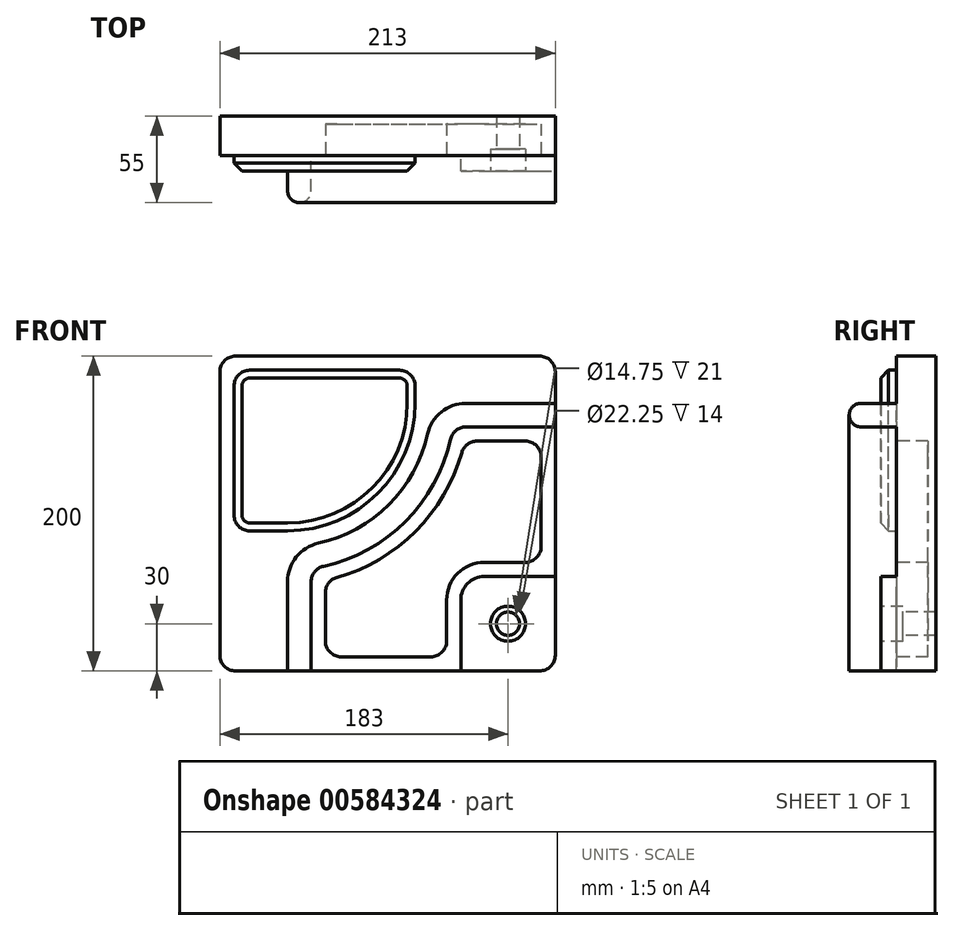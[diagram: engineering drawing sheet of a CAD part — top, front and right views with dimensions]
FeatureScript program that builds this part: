
annotation { "Feature Type Name" : "Feature", "Feature Type Description" : "" }
export const myFeature = defineFeature(function(context is Context, id is Id, definition is map)
    precondition{}
    {
        {
            var Q0;
            Q0=qCreatedBy(makeId("Front.planeOp"),FACE);
            var sketch = newSketch(context, id + "F0", { "sketchPlane" : qUnion([Q0])});
            skLineSegment(sketch, "E0.bottom", {"start": v(-96.5, 100) * mm, "end": v(96.5, 100) * mm});
            skLineSegment(sketch, "E0.top", {"start": v(-96.5, -100) * mm, "end": v(96.5, -100) * mm});
            skLineSegment(sketch, "E0.left", {"start": v(-106.5, 90) * mm, "end": v(-106.5, -90) * mm});
            skLineSegment(sketch, "E0.right", {"start": v(106.5, 90) * mm, "end": v(106.5, -90) * mm});
            skPoint(sketch, "E1.visualSharp", {"position": v(-106.5, -100) * mm});
            skArc(sketch, "E1.filletArc", {"start": v(-106.5, -90) * mm, "mid": v(-103.57, -97.07) * mm, "end": v(-96.5, -100) * mm});
            skPoint(sketch, "E2.visualSharp", {"position": v(106.5, 100) * mm});
            skArc(sketch, "E2.filletArc", {"start": v(106.5, 90) * mm, "mid": v(103.57, 97.07) * mm, "end": v(96.5, 100) * mm});
            skPoint(sketch, "E3.visualSharp", {"position": v(-106.5, 100) * mm});
            skArc(sketch, "E3.filletArc", {"start": v(-96.5, 100) * mm, "mid": v(-103.57, 97.07) * mm, "end": v(-106.5, 90) * mm});
            skPoint(sketch, "E4.visualSharp", {"position": v(106.5, -100) * mm});
            skArc(sketch, "E4.filletArc", {"start": v(96.5, -100) * mm, "mid": v(103.57, -97.07) * mm, "end": v(106.5, -90) * mm});
            skLineSegment(sketch, "E5", {"start": v(106.5, -90) * mm, "end": v(106.5, -91) * mm});
            skLineSegment(sketch, "E6", {"start": v(-106.5, -90) * mm, "end": v(-106.5, -100) * mm});
            skLineSegment(sketch, "E7", {"start": v(-96.5, -100) * mm, "end": v(-106.5, -100) * mm});
            skLineSegment(sketch, "E8", {"start": v(106.5, 90) * mm, "end": v(106.5, -91) * mm});
            skLineSegment(sketch, "E9", {"start": v(-96.5, -100) * mm, "end": v(97.5, -100) * mm});
            skLineSegment(sketch, "E10.bottom", {"start": v(61.5, -40) * mm, "end": v(106.5, -40) * mm});
            skLineSegment(sketch, "E10.top", {"start": v(46.5, -100) * mm, "end": v(97.5, -100) * mm});
            skLineSegment(sketch, "E10.left", {"start": v(46.5, -55) * mm, "end": v(46.5, -100) * mm});
            skLineSegment(sketch, "E10.right", {"start": v(106.5, -40) * mm, "end": v(106.5, -91) * mm});
            skPoint(sketch, "E11.visualSharp", {"position": v(46.5, -40) * mm});
            skArc(sketch, "E11.filletArc", {"start": v(61.5, -40) * mm, "mid": v(50.9, -44.4) * mm, "end": v(46.5, -55) * mm});
            skLineSegment(sketch, "E12", {"start": v(106.5, 70) * mm, "end": v(49.77, 70) * mm});
            skLineSegment(sketch, "E13", {"start": v(-63.5, -100) * mm, "end": v(-63.5, -43.27) * mm});
            skPoint(sketch, "E14.visualSharp", {"position": v(-63.5, -42.85) * mm});
            skPoint(sketch, "E15.visualSharp", {"position": v(49.35, 70) * mm});
            skPoint(sketch, "E16.start.orphan", {"position": v(106.5, 55) * mm});
            skArc(sketch, "E17", {"start": v(-43.89, -18.86) * mm, "mid": v(0.85, 5.65) * mm, "end": v(25.36, 50.39) * mm});
            skPoint(sketch, "E18.visualSharp", {"position": v(-63.5, -21) * mm});
            skArc(sketch, "E18.filletArc", {"start": v(-43.89, -18.86) * mm, "mid": v(-57.99, -27.62) * mm, "end": v(-63.5, -43.27) * mm});
            skPoint(sketch, "E19.visualSharp", {"position": v(27.5, 70) * mm});
            skArc(sketch, "E19.filletArc", {"start": v(49.77, 70) * mm, "mid": v(34.12, 64.49) * mm, "end": v(25.36, 50.39) * mm});
            skLineSegment(sketch, "E20.0", {"start": v(106.5, 55) * mm, "end": v(49.77, 55) * mm});
            skLineSegment(sketch, "E20.1", {"start": v(-48.5, -100) * mm, "end": v(-48.5, -43.27) * mm});
            skArc(sketch, "E20.2", {"start": v(-40.66, -33.5) * mm, "mid": v(-46.3, -37.01) * mm, "end": v(-48.5, -43.27) * mm});
            skArc(sketch, "E20.3", {"start": v(-40.66, -33.5) * mm, "mid": v(11.45, -4.95) * mm, "end": v(40, 47.16) * mm});
            skArc(sketch, "E20.4", {"start": v(49.77, 55) * mm, "mid": v(43.51, 52.8) * mm, "end": v(40, 47.16) * mm});
            skLineSegment(sketch, "E21.0", {"start": v(87.5, 46) * mm, "end": v(56.79, 46) * mm});
            skArc(sketch, "E21.1", {"start": v(-32.22, -40.66) * mm, "mid": v(17.82, -11.32) * mm, "end": v(47.16, 38.72) * mm});
            skLineSegment(sketch, "E21.2", {"start": v(-39.5, -81) * mm, "end": v(-39.5, -50.29) * mm});
            skPoint(sketch, "E22.visualSharp", {"position": v(48.97, 46) * mm});
            skArc(sketch, "E22.filletArc", {"start": v(56.79, 46) * mm, "mid": v(50.75, 43.97) * mm, "end": v(47.16, 38.72) * mm});
            skPoint(sketch, "E23.visualSharp", {"position": v(-39.5, -42.47) * mm});
            skArc(sketch, "E23.filletArc", {"start": v(-32.22, -40.66) * mm, "mid": v(-37.47, -44.25) * mm, "end": v(-39.5, -50.29) * mm});
            skLineSegment(sketch, "E24.0", {"start": v(97.5, 36) * mm, "end": v(97.5, -21) * mm});
            skLineSegment(sketch, "E25.0", {"start": v(61.5, -31) * mm, "end": v(87.5, -31) * mm});
            skArc(sketch, "E26.0", {"start": v(61.5, -31) * mm, "mid": v(44.53, -38.03) * mm, "end": v(37.5, -55) * mm});
            skLineSegment(sketch, "E27.0", {"start": v(37.5, -55) * mm, "end": v(37.5, -81) * mm});
            skLineSegment(sketch, "E28.trimOffspring", {"start": v(-29.5, -91) * mm, "end": v(27.5, -91) * mm});
            skLineSegment(sketch, "E29.trimOffspring", {"start": v(106.45, -91) * mm, "end": v(106.5, -91) * mm});
            skLineSegment(sketch, "E30.trimOffspring", {"start": v(97.5, -99.95) * mm, "end": v(97.5, -100) * mm});
            skPoint(sketch, "E31.visualSharp", {"position": v(-39.5, -91) * mm});
            skArc(sketch, "E31.filletArc", {"start": v(-39.5, -81) * mm, "mid": v(-36.57, -88.07) * mm, "end": v(-29.5, -91) * mm});
            skPoint(sketch, "E32.visualSharp", {"position": v(37.5, -91) * mm});
            skArc(sketch, "E32.filletArc", {"start": v(27.5, -91) * mm, "mid": v(34.57, -88.07) * mm, "end": v(37.5, -81) * mm});
            skPoint(sketch, "E33.visualSharp", {"position": v(97.5, -31) * mm});
            skArc(sketch, "E33.filletArc", {"start": v(87.5, -31) * mm, "mid": v(94.57, -28.07) * mm, "end": v(97.5, -21) * mm});
            skPoint(sketch, "E34.visualSharp", {"position": v(97.5, 46) * mm});
            skArc(sketch, "E34.filletArc", {"start": v(97.5, 36) * mm, "mid": v(94.57, 43.07) * mm, "end": v(87.5, 46) * mm});
            skArc(sketch, "E35", {"start": v(-63.5, -11) * mm, "mid": v(-6.22, 12.72) * mm, "end": v(17.5, 70) * mm});
            skLineSegment(sketch, "E36", {"start": v(17.5, 70) * mm, "end": v(17.5, 81) * mm});
            skLineSegment(sketch, "E37", {"start": v(-63.5, -11) * mm, "end": v(-87.5, -11) * mm});
            skPoint(sketch, "E38.orphan", {"position": v(11.74, 100) * mm});
            skArc(sketch, "E39.0", {"start": v(97.5, 90) * mm, "mid": v(97.2, 90.7) * mm, "end": v(96.5, 91) * mm});
            skLineSegment(sketch, "E39.1", {"start": v(-87.5, 91) * mm, "end": v(7.5, 91) * mm});
            skLineSegment(sketch, "E39.3", {"start": v(-97.5, 81) * mm, "end": v(-97.5, -1) * mm});
            skPoint(sketch, "E40.orphan", {"position": v(17.5, 100) * mm});
            skPoint(sketch, "E41.visualSharp", {"position": v(17.5, 91) * mm});
            skArc(sketch, "E41.filletArc", {"start": v(17.5, 81) * mm, "mid": v(14.57, 88.07) * mm, "end": v(7.5, 91) * mm});
            skPoint(sketch, "E42.visualSharp", {"position": v(-97.5, 91) * mm});
            skArc(sketch, "E42.filletArc", {"start": v(-87.5, 91) * mm, "mid": v(-94.57, 88.07) * mm, "end": v(-97.5, 81) * mm});
            skPoint(sketch, "E43.visualSharp", {"position": v(-97.5, -11) * mm});
            skArc(sketch, "E43.filletArc", {"start": v(-97.5, -1) * mm, "mid": v(-94.57, -8.07) * mm, "end": v(-87.5, -11) * mm});
            skLineSegment(sketch, "E44.bottom", {"start": v(106.5, -100) * mm, "end": v(46.5, -100) * mm});
            skLineSegment(sketch, "E44.top", {"start": v(106.5, -40) * mm, "end": v(61.5, -40) * mm});
            skLineSegment(sketch, "E44.left", {"start": v(106.5, -100) * mm, "end": v(106.5, -40) * mm});
            skLineSegment(sketch, "E44.right", {"start": v(46.5, -100) * mm, "end": v(46.5, -55) * mm});
            skPoint(sketch, "E45", {"position": v(76.5, -70) * mm});
            skPoint(sketch, "E45.positionSnap0", {"position": v(46.5, -70) * mm});
            skPoint(sketch, "E45.positionSnap1", {"position": v(76.5, -40) * mm});
            skSolve(sketch);
        }
        {
            var Q0;
            Q0 = qSketchRegion(id + "F0", true);
            var Q1;
            Q1=makeQuery(id+"F0.imprint","IMPRINT",FACE,{"disambiguationData":[TD([[makeQuery(id+"F0.imprint","IMPRINT",EDGE,{"derivedFrom":sQuery(id+"F0.wireOp",EDGE,"E35")}),1.0]])]});
            var Q2;
            Q2=makeQuery(id+"F0.imprint","IMPRINT",FACE,{"disambiguationData":[TD([[makeQuery(id+"F0.imprint","IMPRINT",EDGE,{"derivedFrom":sQuery(id+"F0.wireOp",EDGE,"E21.0")}),1.0]])]});
            extrude(context, id + "F1", {"entities" : qUnion([Q0, Q1, Q2]), "oppositeDirection" : true, "depth" : 25 * mm, "offsetDistance" : 25 * mm});
        }
        {
            var Q0;
            Q0=makeQuery(id+"F0.imprint","IMPRINT",FACE,{"disambiguationData":[TD([[makeQuery(id+"F0.imprint","IMPRINT",EDGE,{"derivedFrom":sQuery(id+"F0.wireOp",EDGE,"E35")}),1.0]])]});
            extrude(context, id + "F2", {"entities" : qUnion([Q0]), "operationType" : NewBodyOperationType.ADD, "depth" : 10 * mm, "offsetDistance" : 25 * mm});
        }
        {
            var Q0;
            Q0=makeQuery(id+"F0.imprint","IMPRINT",FACE,{"disambiguationData":[TD([[makeQuery(id+"F0.imprint","IMPRINT",EDGE,{"derivedFrom":sQuery(id+"F0.wireOp",EDGE,"E21.0")}),1.0]])]});
            extrude(context, id + "F3", {"entities" : qUnion([Q0]), "operationType" : NewBodyOperationType.REMOVE, "oppositeDirection" : true, "depth" : 20 * mm, "offsetDistance" : 25 * mm});
        }
        {
            var Q0;
            {var subQ2=sQuery(id+"F0.wireOp",EDGE,"E12");Q0=makeQuery(id+"F0.imprint","IMPRINT",FACE,{"disambiguationData":[TD([[makeQuery(id+"F0.imprint","IMPRINT",EDGE,{"derivedFrom":subQ2}),1.0]])]});}
            extrude(context, id + "F4", {"entities" : qUnion([Q0]), "operationType" : NewBodyOperationType.ADD, "depth" : 30 * mm, "offsetDistance" : 25 * mm});
        }
        {
            var Q0;
            Q0=makeQuery(id+"F4.opExtrude","CAP_EDGE",EDGE,{"disambiguationData":[OSD([sQuery(id+"F0.wireOp",EDGE,"E13")])],"isStart":false});
            var Q1;
            Q1=makeQuery(id+"F4.opExtrude","CAP_EDGE",EDGE,{"disambiguationData":[OSD([sQuery(id+"F0.wireOp",EDGE,"E20.1")])],"isStart":false});
            fillet(context, id + "F5", {"entities" : qUnion([Q0, Q1]), "radius" : 7.5 * mm, "tangentPropagation" : true, "allowEdgeOverflow" : false});
        }
        {
            var Q0;
            Q0=makeQuery(id+"F2.opExtrude","CAP_EDGE",EDGE,{"disambiguationData":[OSD([sQuery(id+"F0.wireOp",EDGE,"E39.3")])],"isStart":false});
            chamfer(context, id + "F6", {"entities" : qUnion([Q0]), "width" : 5 * mm, "tangentPropagation" : true});
        }
        {
            var Q0;
            Q0=makeQuery(id+"F1.opExtrude","SWEPT_EDGE",EDGE,{"disambiguationData":[OSD([sQuery(id+"F0.wireOp",EDGE,"E6"),sQuery(id+"F0.wireOp",EDGE,"E7")])]});
            var Q1;
            Q1=makeQuery(id+"F1.opExtrude","SWEPT_EDGE",EDGE,{"disambiguationData":[OSD([sQuery(id+"F0.wireOp",EDGE,"E44.bottom"),sQuery(id+"F0.wireOp",EDGE,"E44.left")])]});
            fillet(context, id + "F7", {"entities" : qUnion([Q0, Q1]), "radius" : 10 * mm, "tangentPropagation" : true, "allowEdgeOverflow" : false});
        }
        {
            var Q0;
            Q0=makeQuery(id+"F0.imprint","IMPRINT",FACE,{"disambiguationData":[TD([[makeQuery(id+"F0.imprint","IMPRINT",EDGE,{"derivedFrom":sQuery(id+"F0.wireOp",EDGE,"E11.filletArc")}),1.0]])]});
            extrude(context, id + "F8", {"entities" : qUnion([Q0]), "operationType" : NewBodyOperationType.ADD, "depth" : 10 * mm, "offsetDistance" : 25 * mm});
        }
        {
            var Q0;
            Q0=makeQuery(id+"F8.opExtrude","CAP_FACE",FACE,{"disambiguationData":[OSD([sQuery(id+"F0.wireOp",EDGE,"E4.filletArc"),sQuery(id+"F0.wireOp",EDGE,"E11.filletArc"),sQuery(id+"F0.wireOp",EDGE,"E44.bottom"),sQuery(id+"F0.wireOp",EDGE,"E44.top"),sQuery(id+"F0.wireOp",EDGE,"E44.left"),sQuery(id+"F0.wireOp",EDGE,"E44.right")])],"isStart":false});
            var sketch = newSketch(context, id + "F9", { "sketchPlane" : qUnion([Q0])});
            skPoint(sketch, "E46", {"position": v(76.5, -70) * mm});
            skSolve(sketch);
        }
        {
            var Q0;
            Q0=sQuery(id+"F9.wireOp",VERTEX,"E46");
            var Q1;
            Q1=makeQuery(id+"F1.opExtrude","SWEPT_BODY",BODY,{"disambiguationData":[OSD([sQuery(id+"F0.wireOp",EDGE,"E0.bottom"),sQuery(id+"F0.wireOp",EDGE,"E0.left"),sQuery(id+"F0.wireOp",EDGE,"E2.filletArc"),sQuery(id+"F0.wireOp",EDGE,"E3.filletArc"),sQuery(id+"F0.wireOp",EDGE,"E6"),sQuery(id+"F0.wireOp",EDGE,"E7"),sQuery(id+"F0.wireOp",EDGE,"E8"),sQuery(id+"F0.wireOp",EDGE,"E9"),sQuery(id+"F0.wireOp",EDGE,"E44.bottom"),sQuery(id+"F0.wireOp",EDGE,"E44.left")])]});
            hole(context, id + "F10", {"style" : HoleStyle.C_BORE, "endStyle" : HoleEndStyle.THROUGH, "standardTappedOrClearance" : lookupTablePath({ "standard" : "ISO", "fit" : "Close", "size" : "M14", "type" : "Clearance" }), "standardBlindInLast" : lookupTablePath({ "fit" : "Close", "standard" : "ISO", "size" : "M14", "type" : "Clearance" }), "holeDiameter" : 14.75 * mm, "cBoreDiameter" : 22.25 * mm, "cBoreDepth" : 14 * mm, "majorDiameter" : 14 * mm, "isTappedThrough" : true, "tappedDepth" : 12 * mm, "tapClearance" : 3, "locations" : qUnion([Q0]), "scope" : qUnion([Q1])});
        }
    });
